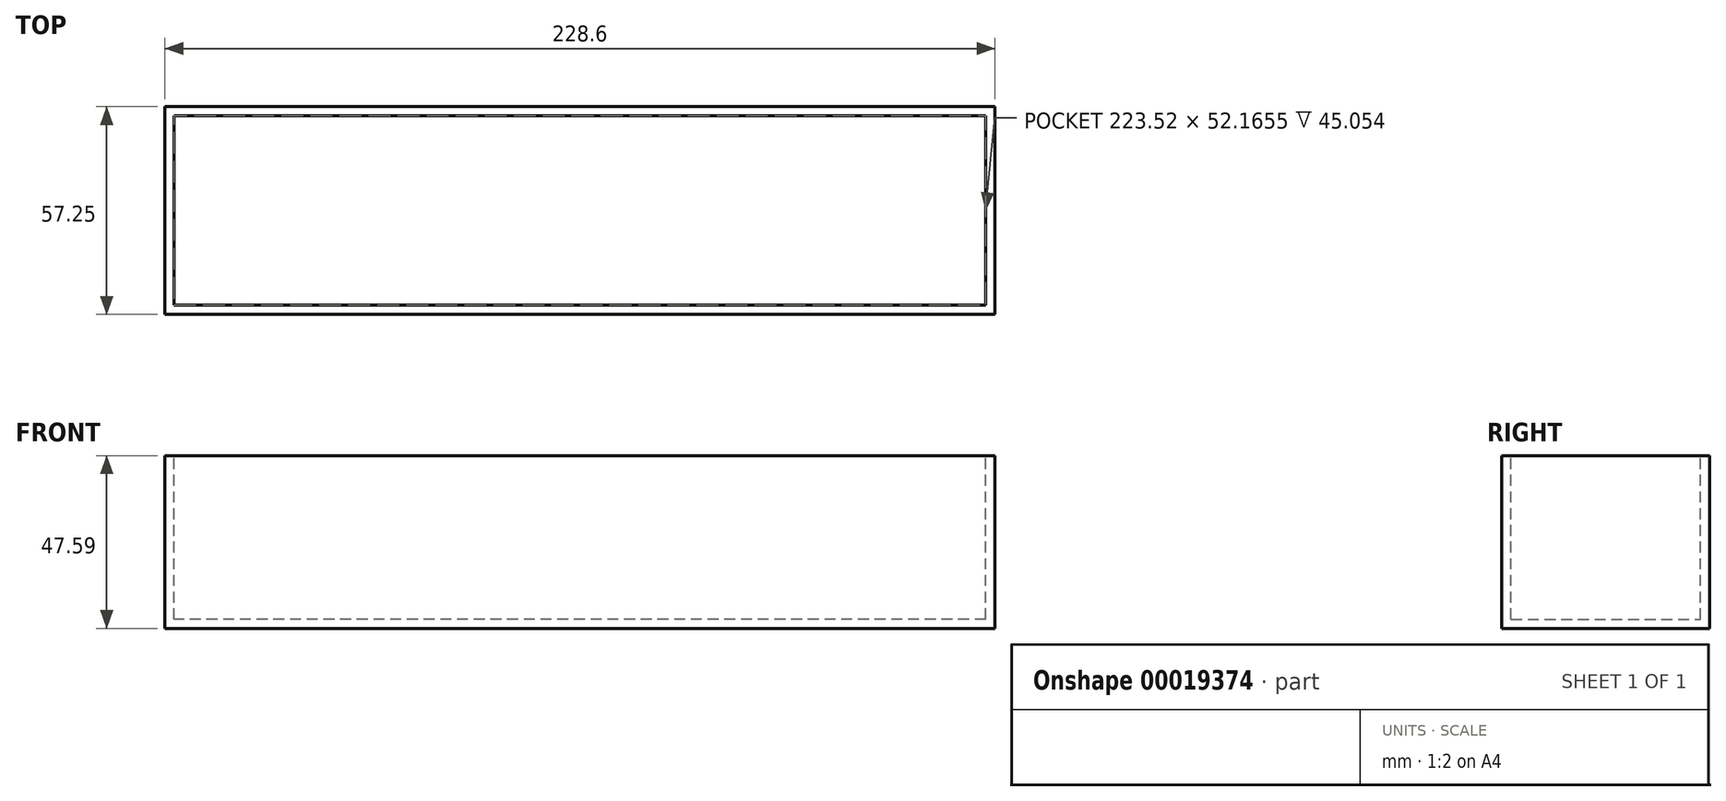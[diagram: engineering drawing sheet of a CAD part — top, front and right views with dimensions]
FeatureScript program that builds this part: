
annotation { "Feature Type Name" : "Feature", "Feature Type Description" : "" }
export const myFeature = defineFeature(function(context is Context, id is Id, definition is map)
    precondition{}
    {
        {
            var Q0;
            Q0=qCreatedBy(makeId("Right.planeOp"),FACE);
            var sketch = newSketch(context, id + "F0", { "sketchPlane" : qUnion([Q0])});
            skLineSegment(sketch, "E0.bottom", {"start": v(0, 0) * mm, "end": v(57.25, 0) * mm});
            skLineSegment(sketch, "E0.top", {"start": v(0, 47.6) * mm, "end": v(57.25, 47.6) * mm});
            skLineSegment(sketch, "E0.left", {"start": v(0, 0) * mm, "end": v(0, 47.6) * mm});
            skLineSegment(sketch, "E0.right", {"start": v(57.25, 0) * mm, "end": v(57.25, 47.6) * mm});
            skSolve(sketch);
        }
        {
            var Q0;
            Q0=makeQuery(id+"F0.imprint","IMPRINT",FACE,{"disambiguationData":[TD([[makeQuery(id+"F0.imprint","IMPRINT",EDGE,{"derivedFrom":sQuery(id+"F0.wireOp",EDGE,"E0.bottom")}),1.0]])]});
            extrude(context, id + "F1", {"entities" : qUnion([Q0]), "depth" : 228.6 * mm});
        }
        {
            var Q0;
            Q0=makeQuery(id+"F1.opExtrude","SWEPT_FACE",FACE,{"disambiguationData":[OSD([sQuery(id+"F0.wireOp",EDGE,"E0.top")])]});
            shell(context, id + "F2", {"entities" : qUnion([Q0]), "thickness" : 2.54 * mm});
        }
    });
